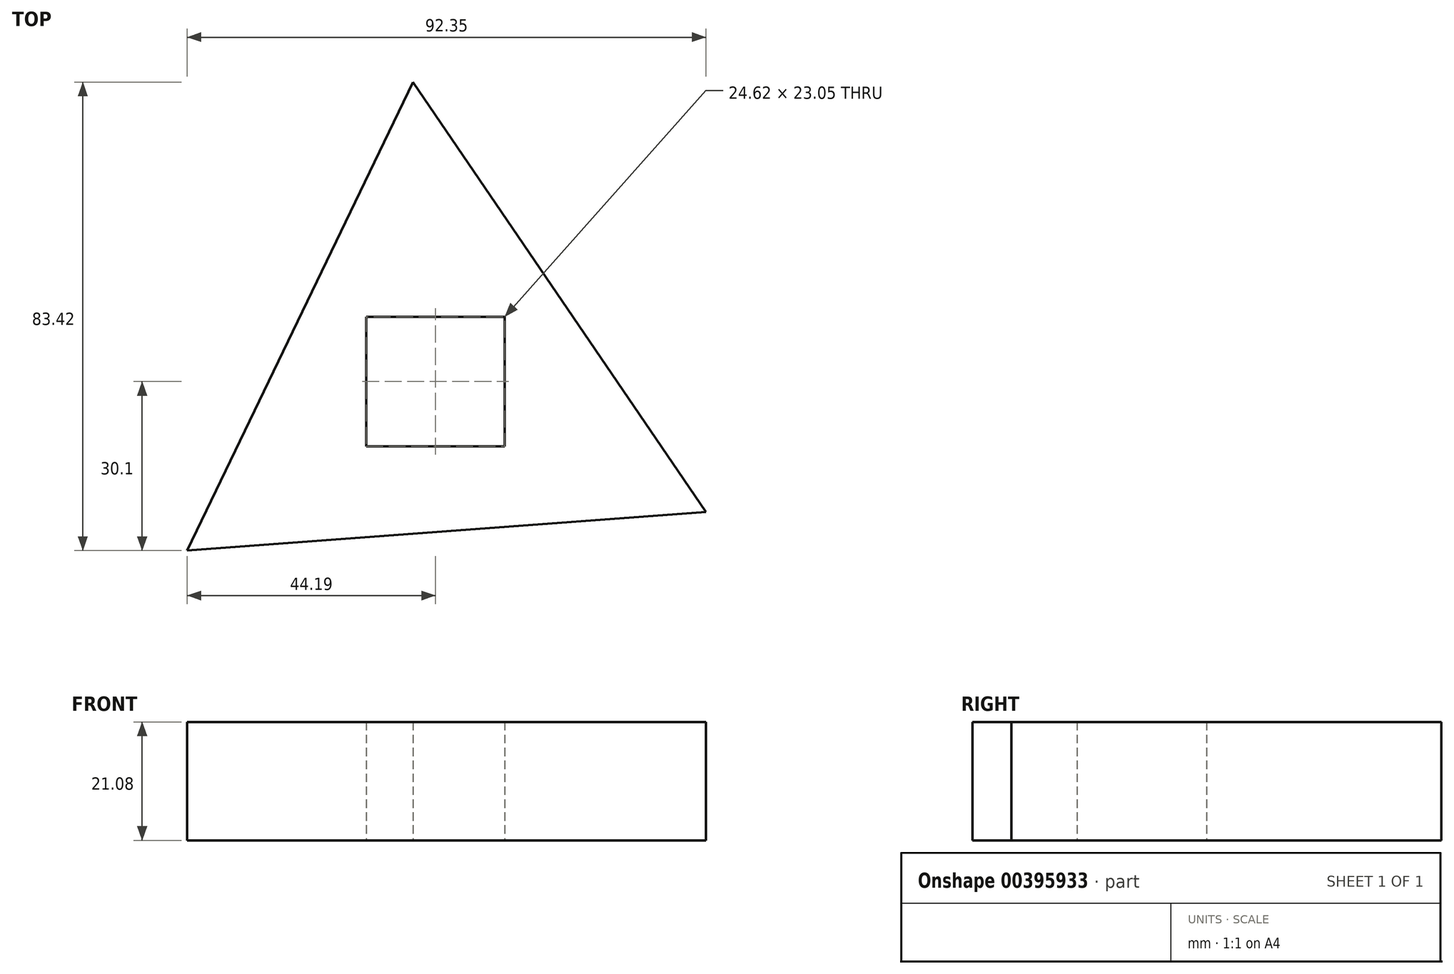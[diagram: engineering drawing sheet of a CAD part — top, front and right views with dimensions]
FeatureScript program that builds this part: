
annotation { "Feature Type Name" : "Feature", "Feature Type Description" : "" }
export const myFeature = defineFeature(function(context is Context, id is Id, definition is map)
    precondition{}
    {
        {
            var Q0;
            Q0=qCreatedBy(makeId("Top.planeOp"),FACE);
            var sketch = newSketch(context, id + "F0", { "sketchPlane" : qUnion([Q0])});
            skCircle(sketch, "E0.cCircle", {"center": v(0, 0) * mm, "radius": 26.73 * mm, "construction": true});
            skLineSegment(sketch, "E0.0", {"start": v(-44.19, -30.1) * mm, "end": v(-3.98, 53.32) * mm});
            skLineSegment(sketch, "E0.1", {"start": v(-3.98, 53.32) * mm, "end": v(48.16, -23.21) * mm});
            skLineSegment(sketch, "E0.2", {"start": v(48.16, -23.21) * mm, "end": v(-44.19, -30.1) * mm});
            skPoint(sketch, "E0.0.midPoint", {"position": v(-24.08, 11.6) * mm});
            skLineSegment(sketch, "E1.bottom", {"start": v(12.3, -11.53) * mm, "end": v(-12.3, -11.53) * mm});
            skLineSegment(sketch, "E1.top", {"start": v(12.3, 11.53) * mm, "end": v(-12.3, 11.53) * mm});
            skLineSegment(sketch, "E1.left", {"start": v(12.3, -11.53) * mm, "end": v(12.3, 11.53) * mm});
            skLineSegment(sketch, "E1.right", {"start": v(-12.3, -11.53) * mm, "end": v(-12.3, 11.53) * mm});
            skSolve(sketch);
        }
        {
            var Q0;
            Q0=makeQuery(id+"F0.imprint","IMPRINT",FACE,{"disambiguationData":[TD([[makeQuery(id+"F0.imprint","IMPRINT",EDGE,{"derivedFrom":sQuery(id+"F0.wireOp",EDGE,"E0.0")}),-1.0]])]});
            extrude(context, id + "F1", {"entities" : qUnion([Q0]), "depth" : 21.08 * mm});
        }
    });
